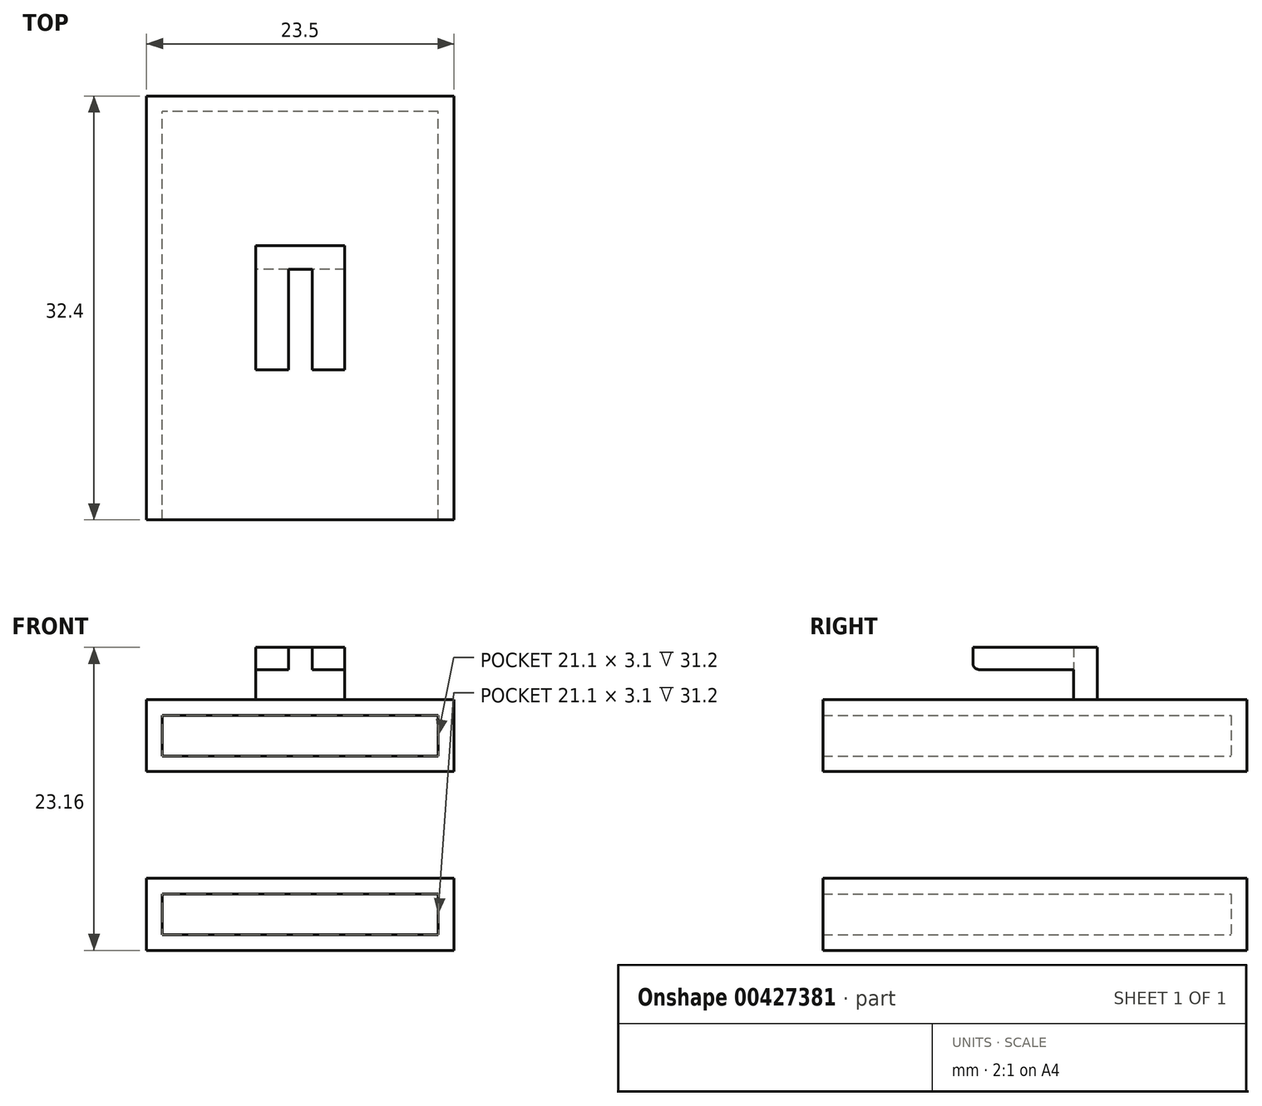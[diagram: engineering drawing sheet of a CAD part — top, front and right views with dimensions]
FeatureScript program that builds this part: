
annotation { "Feature Type Name" : "Feature", "Feature Type Description" : "" }
export const myFeature = defineFeature(function(context is Context, id is Id, definition is map)
    precondition{}
    {
        {
            assignVariable(context, id + "F0", {"name" : "magnet_height", "anyValue" : 30});
        }
        {
            var Q0;
            Q0=qCreatedBy(makeId("Front.planeOp"),FACE);
            var sketch = newSketch(context, id + "F1", { "sketchPlane" : qUnion([Q0])});
            skLineSegment(sketch, "E0.bottom", {"start": v(11.75, 2.75) * mm, "end": v(-11.75, 2.75) * mm});
            skLineSegment(sketch, "E0.top", {"start": v(11.75, -2.75) * mm, "end": v(-11.75, -2.75) * mm});
            skLineSegment(sketch, "E0.left", {"start": v(11.75, 2.75) * mm, "end": v(11.75, -2.75) * mm});
            skLineSegment(sketch, "E0.right", {"start": v(-11.75, 2.75) * mm, "end": v(-11.75, -2.75) * mm});
            skPoint(sketch, "E0.middle", {"position": v(0, 0) * mm});
            skLineSegment(sketch, "E1.bottom", {"start": v(10.55, 1.55) * mm, "end": v(-10.55, 1.55) * mm});
            skLineSegment(sketch, "E1.top", {"start": v(10.55, -1.55) * mm, "end": v(-10.55, -1.55) * mm});
            skLineSegment(sketch, "E1.left", {"start": v(10.55, 1.55) * mm, "end": v(10.55, -1.55) * mm});
            skLineSegment(sketch, "E1.right", {"start": v(-10.55, 1.55) * mm, "end": v(-10.55, -1.55) * mm});
            skSolve(sketch);
        }
        {
            var Q0;
            Q0=makeQuery(id+"F1.imprint","IMPRINT",FACE,{"disambiguationData":[TD([[makeQuery(id+"F1.imprint","IMPRINT",EDGE,{"derivedFrom":sQuery(id+"F1.wireOp",EDGE,"E0.bottom")}),1.0]])]});
            extrude(context, id + "F2", {"entities" : qUnion([Q0]), "depth" : (getVariable(context, 'magnet_height') + 2.4) * mm});
        }
        {
            var Q0;
            Q0=makeQuery(id+"F1.imprint","IMPRINT",FACE,{"disambiguationData":[TD([[makeQuery(id+"F1.imprint","IMPRINT",EDGE,{"derivedFrom":sQuery(id+"F1.wireOp",EDGE,"E1.bottom")}),1.0]])]});
            extrude(context, id + "F3", {"entities" : qUnion([Q0]), "operationType" : NewBodyOperationType.ADD, "depth" : 1.2 * mm});
        }
        {
            var Q0;
            Q0=qCreatedBy(makeId("Front.planeOp"),FACE);
            var sketch = newSketch(context, id + "F4", { "sketchPlane" : qUnion([Q0])});
            skLineSegment(sketch, "E2.bottom", {"start": v(11.75, 16.4) * mm, "end": v(-11.75, 16.4) * mm});
            skLineSegment(sketch, "E2.top", {"start": v(11.75, 10.9) * mm, "end": v(-11.75, 10.9) * mm});
            skLineSegment(sketch, "E2.left", {"start": v(11.75, 16.4) * mm, "end": v(11.75, 10.9) * mm});
            skLineSegment(sketch, "E2.right", {"start": v(-11.75, 16.4) * mm, "end": v(-11.75, 10.9) * mm});
            skPoint(sketch, "E2.middle", {"position": v(0, 13.66) * mm});
            skLineSegment(sketch, "E3.bottom", {"start": v(10.55, 15.2) * mm, "end": v(-10.55, 15.2) * mm});
            skLineSegment(sketch, "E3.top", {"start": v(10.55, 12.1) * mm, "end": v(-10.55, 12.1) * mm});
            skLineSegment(sketch, "E3.left", {"start": v(10.55, 15.2) * mm, "end": v(10.55, 12.1) * mm});
            skLineSegment(sketch, "E3.right", {"start": v(-10.55, 15.2) * mm, "end": v(-10.55, 12.1) * mm});
            skSolve(sketch);
        }
        {
            var Q0;
            Q0=makeQuery(id+"F4.imprint","IMPRINT",FACE,{"disambiguationData":[TD([[makeQuery(id+"F4.imprint","IMPRINT",EDGE,{"derivedFrom":sQuery(id+"F4.wireOp",EDGE,"E3.bottom")}),1.0]])]});
            extrude(context, id + "F5", {"entities" : qUnion([Q0]), "depth" : 1.2 * mm});
        }
        {
            var Q0;
            Q0=makeQuery(id+"F4.imprint","IMPRINT",FACE,{"disambiguationData":[TD([[makeQuery(id+"F4.imprint","IMPRINT",EDGE,{"derivedFrom":sQuery(id+"F4.wireOp",EDGE,"E2.bottom")}),1.0]])]});
            var Q1;
            Q1=makeQuery(id+"F2.opExtrude","CAP_FACE",FACE,{"disambiguationData":[OSD([sQuery(id+"F1.wireOp",EDGE,"E0.bottom"),sQuery(id+"F1.wireOp",EDGE,"E0.top"),sQuery(id+"F1.wireOp",EDGE,"E0.left"),sQuery(id+"F1.wireOp",EDGE,"E0.right"),sQuery(id+"F1.wireOp",EDGE,"E1.bottom"),sQuery(id+"F1.wireOp",EDGE,"E1.top"),sQuery(id+"F1.wireOp",EDGE,"E1.left"),sQuery(id+"F1.wireOp",EDGE,"E1.right")])],"isStart":false});
            extrude(context, id + "F6", {"entities" : qUnion([Q0]), "operationType" : NewBodyOperationType.ADD, "endBound" : BoundingType.UP_TO_SURFACE, "endBoundEntityFace" : qUnion([Q1]), "depth" : 25 * mm});
        }
        {
            var Q0;
            Q0=makeQuery(id+"F6.opExtrude","SWEPT_FACE",FACE,{"disambiguationData":[OSD([sQuery(id+"F4.wireOp",EDGE,"E2.bottom")])]});
            var sketch = newSketch(context, id + "F7", { "sketchPlane" : qUnion([Q0])});
            skLineSegment(sketch, "E4.bottom", {"start": v(-3.4, -20.95) * mm, "end": v(3.4, -20.95) * mm});
            skLineSegment(sketch, "E4.top", {"start": v(-3.4, -11.45) * mm, "end": v(3.4, -11.45) * mm});
            skLineSegment(sketch, "E4.left", {"start": v(-3.4, -20.95) * mm, "end": v(-3.4, -11.45) * mm});
            skLineSegment(sketch, "E4.right", {"start": v(3.4, -20.95) * mm, "end": v(3.4, -11.45) * mm});
            skPoint(sketch, "E4.middle", {"position": v(0, -16.2) * mm});
            skLineSegment(sketch, "E5", {"start": v(0, 0) * mm, "end": v(0, -32.4) * mm, "construction": true});
            skLineSegment(sketch, "E6", {"start": v(3.4, -13.25) * mm, "end": v(-3.4, -13.25) * mm});
            skLineSegment(sketch, "E7.bottom", {"start": v(0.9, -13.25) * mm, "end": v(-0.9, -13.25) * mm});
            skLineSegment(sketch, "E7.top", {"start": v(0.9, -20.95) * mm, "end": v(-0.9, -20.95) * mm});
            skLineSegment(sketch, "E7.left", {"start": v(0.9, -13.25) * mm, "end": v(0.9, -20.95) * mm});
            skLineSegment(sketch, "E7.right", {"start": v(-0.9, -13.25) * mm, "end": v(-0.9, -20.95) * mm});
            skLineSegment(sketch, "E8", {"start": v(0.9, -17.75) * mm, "end": v(-0.9, -17.75) * mm, "construction": true});
            skPoint(sketch, "E9", {"position": v(0, -17.75) * mm});
            skSolve(sketch);
        }
        {
            var Q0;
            {var subQ3=sQuery(id+"F7.wireOp",EDGE,"E7.left");Q0=makeQuery(id+"F7.imprint","IMPRINT",FACE,{"disambiguationData":[TD([[makeQuery(id+"F7.imprint","IMPRINT",EDGE,{"derivedFrom":subQ3}),1.0]])]});}
            var Q1;
            {var subQ3=sQuery(id+"F7.wireOp",EDGE,"E7.right");Q1=makeQuery(id+"F7.imprint","IMPRINT",FACE,{"disambiguationData":[TD([[makeQuery(id+"F7.imprint","IMPRINT",EDGE,{"derivedFrom":subQ3}),-1.0]])]});}
            extrude(context, id + "F8", {"entities" : qUnion([Q0, Q1]), "depth" : 4 * mm, "hasSecondDirection" : true, "secondDirectionOppositeDirection" : false, "secondDirectionDepth" : 2.3 * mm});
        }
        {
            var Q0;
            Q0=makeQuery(id+"F7.imprint","IMPRINT",FACE,{"disambiguationData":[TD([[makeQuery(id+"F7.imprint","IMPRINT",EDGE,{"derivedFrom":sQuery(id+"F7.wireOp",EDGE,"E7.bottom")}),1.0]])]});
            var Q1;
            {var subQ1=sQuery(id+"F7.wireOp",EDGE,"E4.top");Q1=makeQuery(id+"F7.imprint","IMPRINT",FACE,{"disambiguationData":[TD([[makeQuery(id+"F7.imprint","IMPRINT",EDGE,{"derivedFrom":subQ1}),-1.0]])]});}
            extrude(context, id + "F9", {"entities" : qUnion([Q0, Q1]), "operationType" : NewBodyOperationType.ADD, "depth" : 4 * mm});
        }
        {
            var Q0;
            {var subQ0=sQuery(id+"F7.wireOp",EDGE,"E4.bottom");Q0=makeQuery(id+"F8.opExtrude","CAP_EDGE",EDGE,{"disambiguationData":[OSD([subQ0]),TDD([makeQuery(id+"F7.imprint","IMPRINT",EDGE,{"disambiguationData":[TD([[makeQuery(id+"F7.imprint","INTERSECT",VERTEX,{"derivedFrom":[subQ0,sQuery(id+"F7.wireOp",EDGE,"E4.left")]}),-1.0]])],"derivedFrom":subQ0})])],"isStart":true});}
            var Q1;
            {var subQ0=sQuery(id+"F7.wireOp",EDGE,"E4.bottom");Q1=makeQuery(id+"F8.opExtrude","CAP_EDGE",EDGE,{"disambiguationData":[OSD([subQ0]),TDD([makeQuery(id+"F7.imprint","IMPRINT",EDGE,{"disambiguationData":[TD([[makeQuery(id+"F7.imprint","INTERSECT",VERTEX,{"derivedFrom":[subQ0,sQuery(id+"F7.wireOp",EDGE,"E4.right")]}),1.0]])],"derivedFrom":subQ0})])],"isStart":true});}
            var Q2;
            Q2=makeQuery(id+"F9.opExtrude","SWEPT_EDGE",EDGE,{"disambiguationData":[OSD([sQuery(id+"F7.wireOp",EDGE,"E4.bottom"),sQuery(id+"F7.wireOp",EDGE,"E7.top"),sQuery(id+"F7.wireOp",EDGE,"E7.left")])]});
            var Q3;
            Q3=makeQuery(id+"F9.opExtrude","SWEPT_EDGE",EDGE,{"disambiguationData":[OSD([sQuery(id+"F7.wireOp",EDGE,"E4.bottom"),sQuery(id+"F7.wireOp",EDGE,"E7.top"),sQuery(id+"F7.wireOp",EDGE,"E7.right")])]});
            fillet(context, id + "F10", {"entities" : qUnion([Q0, Q1, Q2, Q3]), "radius" : 0.5 * mm, "tangentPropagation" : true, "allowEdgeOverflow" : false});
        }
    });
